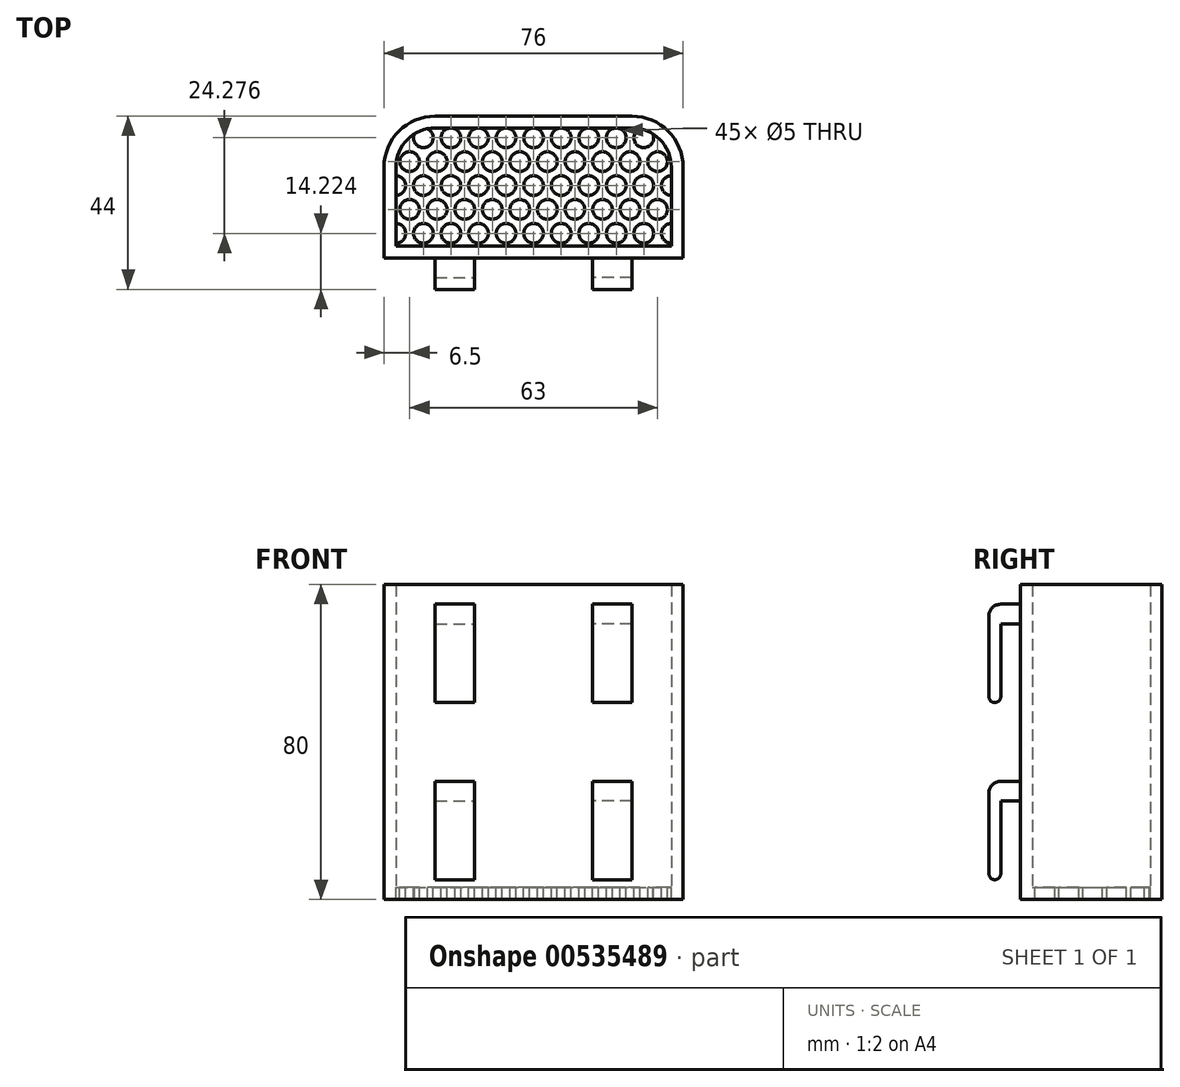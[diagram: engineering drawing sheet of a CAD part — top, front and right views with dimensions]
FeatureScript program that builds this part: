
annotation { "Feature Type Name" : "Feature", "Feature Type Description" : "" }
export const myFeature = defineFeature(function(context is Context, id is Id, definition is map)
    precondition{}
    {
        {
            var Q0;
            Q0=qCreatedBy(makeId("Top.planeOp"),FACE);
            var sketch = newSketch(context, id + "F0", { "sketchPlane" : qUnion([Q0])});
            skLineSegment(sketch, "E0.bottom", {"start": v(-35, -15) * mm, "end": v(35, -15) * mm});
            skLineSegment(sketch, "E0.top", {"start": v(-25, 15) * mm, "end": v(25, 15) * mm});
            skLineSegment(sketch, "E0.left", {"start": v(-35, -15) * mm, "end": v(-35, 5) * mm});
            skLineSegment(sketch, "E0.right", {"start": v(35, -15) * mm, "end": v(35, 5) * mm});
            skPoint(sketch, "E0.middle", {"position": v(0, 0) * mm});
            skPoint(sketch, "E1.visualSharp", {"position": v(-35, 15) * mm});
            skArc(sketch, "E1.filletArc", {"start": v(-25, 15) * mm, "mid": v(-32.07, 12.07) * mm, "end": v(-35, 5) * mm});
            skPoint(sketch, "E2.visualSharp", {"position": v(35, 15) * mm});
            skArc(sketch, "E2.filletArc", {"start": v(35, 5) * mm, "mid": v(32.07, 12.07) * mm, "end": v(25, 15) * mm});
            skLineSegment(sketch, "E3.0", {"start": v(-38, -18) * mm, "end": v(38, -18) * mm});
            skArc(sketch, "E3.1", {"start": v(-25, 18) * mm, "mid": v(-34.2, 14.2) * mm, "end": v(-38, 5) * mm});
            skLineSegment(sketch, "E3.2", {"start": v(-25, 18) * mm, "end": v(25, 18) * mm});
            skLineSegment(sketch, "E3.3", {"start": v(-38, -18) * mm, "end": v(-38, 5) * mm});
            skArc(sketch, "E3.4", {"start": v(38, 5) * mm, "mid": v(34.2, 14.2) * mm, "end": v(25, 18) * mm});
            skLineSegment(sketch, "E3.5", {"start": v(38, -18) * mm, "end": v(38, 5) * mm});
            skSolve(sketch);
        }
        {
            var Q0;
            Q0=makeQuery(id+"F0.imprint","IMPRINT",FACE,{"disambiguationData":[TD([[makeQuery(id+"F0.imprint","IMPRINT",EDGE,{"derivedFrom":sQuery(id+"F0.wireOp",EDGE,"E0.bottom")}),-1.0]])]});
            extrude(context, id + "F1", {"entities" : qUnion([Q0]), "depth" : 80 * mm, "offsetDistance" : 25 * mm});
        }
        {
            var Q0;
            Q0=makeQuery(id+"F0.imprint","IMPRINT",FACE,{"disambiguationData":[TD([[makeQuery(id+"F0.imprint","IMPRINT",EDGE,{"derivedFrom":sQuery(id+"F0.wireOp",EDGE,"E0.bottom")}),1.0]])]});
            extrude(context, id + "F2", {"entities" : qUnion([Q0]), "operationType" : NewBodyOperationType.ADD, "depth" : 3 * mm, "offsetDistance" : 25 * mm});
        }
        {
            var Q0;
            Q0=makeQuery(id+"F2.opExtrude","CAP_FACE",FACE,{"disambiguationData":[OSD([sQuery(id+"F0.wireOp",EDGE,"E0.bottom"),sQuery(id+"F0.wireOp",EDGE,"E0.top"),sQuery(id+"F0.wireOp",EDGE,"E0.left"),sQuery(id+"F0.wireOp",EDGE,"E0.right"),sQuery(id+"F0.wireOp",EDGE,"E1.filletArc"),sQuery(id+"F0.wireOp",EDGE,"E2.filletArc")])],"isStart":false});
            var sketch = newSketch(context, id + "F3", { "sketchPlane" : qUnion([Q0])});
            skCircle(sketch, "E4.1.0.0", {"center": v(-28, 12.5) * mm, "radius": 2.5 * mm});
            skCircle(sketch, "E4.2.0.0", {"center": v(-21, 12.5) * mm, "radius": 2.5 * mm});
            skCircle(sketch, "E4.3.0.0", {"center": v(-14, 12.5) * mm, "radius": 2.5 * mm});
            skCircle(sketch, "E4.4.0.0", {"center": v(-7, 12.5) * mm, "radius": 2.5 * mm});
            skCircle(sketch, "E4.5.0.0", {"center": v(0, 12.5) * mm, "radius": 2.5 * mm});
            skCircle(sketch, "E4.6.0.0", {"center": v(7, 12.5) * mm, "radius": 2.5 * mm});
            skCircle(sketch, "E4.7.0.0", {"center": v(14, 12.5) * mm, "radius": 2.5 * mm});
            skCircle(sketch, "E4.8.0.0", {"center": v(21, 12.5) * mm, "radius": 2.5 * mm});
            skLineSegment(sketch, "E4.direction1", {"start": v(-35, 12.5) * mm, "end": v(-28, 12.5) * mm, "construction": true});
            skCircle(sketch, "E5.0.9.0", {"center": v(28, 12.5) * mm, "radius": 2.5 * mm});
            skCircle(sketch, "E6.1.0.0", {"center": v(10.5, 6.44) * mm, "radius": 2.5 * mm});
            skCircle(sketch, "E6.1.0.1", {"center": v(-24.5, 6.44) * mm, "radius": 2.5 * mm});
            skCircle(sketch, "E6.1.0.2", {"center": v(-3.5, 6.44) * mm, "radius": 2.5 * mm});
            skCircle(sketch, "E6.1.0.3", {"center": v(24.5, 6.44) * mm, "radius": 2.5 * mm});
            skCircle(sketch, "E6.1.0.4", {"center": v(-17.5, 6.44) * mm, "radius": 2.5 * mm});
            skCircle(sketch, "E6.1.0.5", {"center": v(17.5, 6.44) * mm, "radius": 2.5 * mm});
            skCircle(sketch, "E6.1.0.6", {"center": v(3.5, 6.44) * mm, "radius": 2.5 * mm});
            skCircle(sketch, "E6.1.0.8", {"center": v(-31.5, 6.44) * mm, "radius": 2.5 * mm});
            skCircle(sketch, "E6.1.0.9", {"center": v(31.5, 6.44) * mm, "radius": 2.5 * mm});
            skCircle(sketch, "E6.1.0.10", {"center": v(-10.5, 6.44) * mm, "radius": 2.5 * mm});
            skLineSegment(sketch, "E6.1.0.11", {"start": v(-31.5, 6.44) * mm, "end": v(-24.5, 6.44) * mm, "construction": true});
            skLineSegment(sketch, "E6.direction1", {"start": v(-35, 12.5) * mm, "end": v(-31.5, 6.44) * mm, "construction": true});
            skLineSegment(sketch, "E7", {"start": v(-3.5, 6.44) * mm, "end": v(3.5, 6.44) * mm, "construction": true});
            skLineSegment(sketch, "E8", {"start": v(-31.5, 6.44) * mm, "end": v(-28, 12.5) * mm, "construction": true});
            skCircle(sketch, "E9.1.0.0", {"center": v(31.5, -5.7) * mm, "radius": 2.5 * mm});
            skLineSegment(sketch, "E9.1.0.1", {"start": v(-31.5, -5.7) * mm, "end": v(-24.5, -5.7) * mm, "construction": true});
            skCircle(sketch, "E9.1.0.2", {"center": v(28, 0.36) * mm, "radius": 2.5 * mm});
            skLineSegment(sketch, "E9.1.0.3", {"start": v(-35, 0.36) * mm, "end": v(-28, 0.36) * mm, "construction": true});
            skCircle(sketch, "E9.1.0.4", {"center": v(-14, 0.36) * mm, "radius": 2.5 * mm});
            skCircle(sketch, "E9.1.0.5", {"center": v(-31.5, -5.7) * mm, "radius": 2.5 * mm});
            skCircle(sketch, "E9.1.0.6", {"center": v(-7, 0.36) * mm, "radius": 2.5 * mm});
            skCircle(sketch, "E9.1.0.7", {"center": v(0, 0.36) * mm, "radius": 2.5 * mm});
            skCircle(sketch, "E9.1.0.8", {"center": v(35, 0.36) * mm, "radius": 2.5 * mm});
            skCircle(sketch, "E9.1.0.9", {"center": v(10.5, -5.7) * mm, "radius": 2.5 * mm});
            skCircle(sketch, "E9.1.0.10", {"center": v(-21, 0.36) * mm, "radius": 2.5 * mm});
            skCircle(sketch, "E9.1.0.11", {"center": v(-28, 0.36) * mm, "radius": 2.5 * mm});
            skCircle(sketch, "E9.1.0.12", {"center": v(-10.5, -5.7) * mm, "radius": 2.5 * mm});
            skCircle(sketch, "E9.1.0.13", {"center": v(17.5, -5.7) * mm, "radius": 2.5 * mm});
            skCircle(sketch, "E9.1.0.14", {"center": v(-24.5, -5.7) * mm, "radius": 2.5 * mm});
            skCircle(sketch, "E9.1.0.15", {"center": v(7, 0.36) * mm, "radius": 2.5 * mm});
            skCircle(sketch, "E9.1.0.16", {"center": v(-3.5, -5.7) * mm, "radius": 2.5 * mm});
            skLineSegment(sketch, "E9.1.0.17", {"start": v(-3.5, -5.7) * mm, "end": v(3.5, -5.7) * mm, "construction": true});
            skCircle(sketch, "E9.1.0.18", {"center": v(24.5, -5.7) * mm, "radius": 2.5 * mm});
            skCircle(sketch, "E9.1.0.19", {"center": v(-35, 0.36) * mm, "radius": 2.5 * mm});
            skCircle(sketch, "E9.1.0.20", {"center": v(14, 0.36) * mm, "radius": 2.5 * mm});
            skCircle(sketch, "E9.1.0.21", {"center": v(21, 0.36) * mm, "radius": 2.5 * mm});
            skCircle(sketch, "E9.1.0.22", {"center": v(3.5, -5.7) * mm, "radius": 2.5 * mm});
            skCircle(sketch, "E9.1.0.23", {"center": v(-17.5, -5.7) * mm, "radius": 2.5 * mm});
            skLineSegment(sketch, "E9.1.0.24", {"start": v(-31.5, -5.7) * mm, "end": v(-28, 0.36) * mm, "construction": true});
            skLineSegment(sketch, "E9.1.0.25", {"start": v(-35, 0.36) * mm, "end": v(-31.5, -5.7) * mm, "construction": true});
            skCircle(sketch, "E9.2.0.2", {"center": v(28, -11.78) * mm, "radius": 2.5 * mm});
            skLineSegment(sketch, "E9.2.0.3", {"start": v(-35, -11.78) * mm, "end": v(-28, -11.78) * mm, "construction": true});
            skCircle(sketch, "E9.2.0.4", {"center": v(-14, -11.78) * mm, "radius": 2.5 * mm});
            skCircle(sketch, "E9.2.0.6", {"center": v(-7, -11.78) * mm, "radius": 2.5 * mm});
            skCircle(sketch, "E9.2.0.7", {"center": v(0, -11.78) * mm, "radius": 2.5 * mm});
            skCircle(sketch, "E9.2.0.8", {"center": v(35, -11.78) * mm, "radius": 2.5 * mm});
            skCircle(sketch, "E9.2.0.10", {"center": v(-21, -11.78) * mm, "radius": 2.5 * mm});
            skCircle(sketch, "E9.2.0.11", {"center": v(-28, -11.78) * mm, "radius": 2.5 * mm});
            skCircle(sketch, "E9.2.0.15", {"center": v(7, -11.78) * mm, "radius": 2.5 * mm});
            skCircle(sketch, "E9.2.0.19", {"center": v(-35, -11.78) * mm, "radius": 2.5 * mm});
            skCircle(sketch, "E9.2.0.20", {"center": v(14, -11.78) * mm, "radius": 2.5 * mm});
            skCircle(sketch, "E9.2.0.21", {"center": v(21, -11.78) * mm, "radius": 2.5 * mm});
            skLineSegment(sketch, "E9.direction1", {"start": v(-31.5, 6.44) * mm, "end": v(-31.5, -5.7) * mm, "construction": true});
            skSolve(sketch);
        }
        {
            var Q0;
            {var subQ0=sQuery(id+"F3.wireOp",EDGE,"E4.1.0.0");var subQ1=makeQuery(id+"F2.opExtrude","CAP_EDGE",EDGE,{"disambiguationData":[OSD([sQuery(id+"F0.wireOp",EDGE,"E1.filletArc")])],"isStart":false});var subQ2=makeQuery(id+"F3.imprint","INTERSECT",VERTEX,{"disambiguationData":[OD(0.0)],"derivedFrom":[subQ1,subQ0]});Q0=makeQuery(id+"F3.imprint","IMPRINT",FACE,{"disambiguationData":[TD([[makeQuery(id+"F3.imprint","IMPRINT",EDGE,{"disambiguationData":[TD([[subQ2,1.0]])],"derivedFrom":subQ0}),1.0]])]});}
            var Q1;
            Q1=makeQuery(id+"F3.imprint","IMPRINT",FACE,{"disambiguationData":[TD([[makeQuery(id+"F3.imprint","IMPRINT",EDGE,{"derivedFrom":sQuery(id+"F3.wireOp",EDGE,"E6.1.0.8")}),1.0]])]});
            var Q2;
            Q2=makeQuery(id+"F3.imprint","IMPRINT",FACE,{"disambiguationData":[TD([[makeQuery(id+"F3.imprint","IMPRINT",EDGE,{"derivedFrom":sQuery(id+"F3.wireOp",EDGE,"E9.1.0.11")}),1.0]])]});
            var Q3;
            {var subQ0=sQuery(id+"F3.wireOp",EDGE,"E9.1.0.19");var subQ1=makeQuery(id+"F2.opExtrude","CAP_EDGE",EDGE,{"disambiguationData":[OSD([sQuery(id+"F0.wireOp",EDGE,"E0.left")])],"isStart":false});var subQ2=makeQuery(id+"F3.imprint","INTERSECT",VERTEX,{"disambiguationData":[OD(0.0)],"derivedFrom":[subQ1,subQ0]});Q3=makeQuery(id+"F3.imprint","IMPRINT",FACE,{"disambiguationData":[TD([[makeQuery(id+"F3.imprint","IMPRINT",EDGE,{"disambiguationData":[TD([[subQ2,1.0]])],"derivedFrom":subQ0}),1.0]])]});}
            var Q4;
            Q4=makeQuery(id+"F3.imprint","IMPRINT",FACE,{"disambiguationData":[TD([[makeQuery(id+"F3.imprint","IMPRINT",EDGE,{"derivedFrom":sQuery(id+"F3.wireOp",EDGE,"E9.1.0.5")}),1.0]])]});
            var Q5;
            {var subQ0=sQuery(id+"F3.wireOp",EDGE,"E9.2.0.19");var subQ1=makeQuery(id+"F2.opExtrude","CAP_EDGE",EDGE,{"disambiguationData":[OSD([sQuery(id+"F0.wireOp",EDGE,"E0.left")])],"isStart":false});var subQ2=makeQuery(id+"F3.imprint","INTERSECT",VERTEX,{"disambiguationData":[OD(0.0)],"derivedFrom":[subQ1,subQ0]});Q5=makeQuery(id+"F3.imprint","IMPRINT",FACE,{"disambiguationData":[TD([[makeQuery(id+"F3.imprint","IMPRINT",EDGE,{"disambiguationData":[TD([[subQ2,-1.0]])],"derivedFrom":subQ0}),1.0]])]});}
            var Q6;
            Q6=makeQuery(id+"F3.imprint","IMPRINT",FACE,{"disambiguationData":[TD([[makeQuery(id+"F3.imprint","IMPRINT",EDGE,{"derivedFrom":sQuery(id+"F3.wireOp",EDGE,"E9.2.0.11")}),1.0]])]});
            var Q7;
            Q7=makeQuery(id+"F3.imprint","IMPRINT",FACE,{"disambiguationData":[TD([[makeQuery(id+"F3.imprint","IMPRINT",EDGE,{"derivedFrom":sQuery(id+"F3.wireOp",EDGE,"E9.1.0.14")}),1.0]])]});
            var Q8;
            Q8=makeQuery(id+"F3.imprint","IMPRINT",FACE,{"disambiguationData":[TD([[makeQuery(id+"F3.imprint","IMPRINT",EDGE,{"derivedFrom":sQuery(id+"F3.wireOp",EDGE,"E9.1.0.10")}),1.0]])]});
            var Q9;
            Q9=makeQuery(id+"F3.imprint","IMPRINT",FACE,{"disambiguationData":[TD([[makeQuery(id+"F3.imprint","IMPRINT",EDGE,{"derivedFrom":sQuery(id+"F3.wireOp",EDGE,"E6.1.0.1")}),1.0]])]});
            var Q10;
            Q10=makeQuery(id+"F3.imprint","IMPRINT",FACE,{"disambiguationData":[TD([[makeQuery(id+"F3.imprint","IMPRINT",EDGE,{"derivedFrom":sQuery(id+"F3.wireOp",EDGE,"E4.2.0.0")}),1.0]])]});
            var Q11;
            Q11=makeQuery(id+"F3.imprint","IMPRINT",FACE,{"disambiguationData":[TD([[makeQuery(id+"F3.imprint","IMPRINT",EDGE,{"derivedFrom":sQuery(id+"F3.wireOp",EDGE,"E4.3.0.0")}),1.0]])]});
            var Q12;
            Q12=makeQuery(id+"F3.imprint","IMPRINT",FACE,{"disambiguationData":[TD([[makeQuery(id+"F3.imprint","IMPRINT",EDGE,{"derivedFrom":sQuery(id+"F3.wireOp",EDGE,"E4.4.0.0")}),1.0]])]});
            var Q13;
            Q13=makeQuery(id+"F3.imprint","IMPRINT",FACE,{"disambiguationData":[TD([[makeQuery(id+"F3.imprint","IMPRINT",EDGE,{"derivedFrom":sQuery(id+"F3.wireOp",EDGE,"E4.5.0.0")}),1.0]])]});
            var Q14;
            Q14=makeQuery(id+"F3.imprint","IMPRINT",FACE,{"disambiguationData":[TD([[makeQuery(id+"F3.imprint","IMPRINT",EDGE,{"derivedFrom":sQuery(id+"F3.wireOp",EDGE,"E4.6.0.0")}),1.0]])]});
            var Q15;
            Q15=makeQuery(id+"F3.imprint","IMPRINT",FACE,{"disambiguationData":[TD([[makeQuery(id+"F3.imprint","IMPRINT",EDGE,{"derivedFrom":sQuery(id+"F3.wireOp",EDGE,"E4.7.0.0")}),1.0]])]});
            var Q16;
            Q16=makeQuery(id+"F3.imprint","IMPRINT",FACE,{"disambiguationData":[TD([[makeQuery(id+"F3.imprint","IMPRINT",EDGE,{"derivedFrom":sQuery(id+"F3.wireOp",EDGE,"E4.8.0.0")}),1.0]])]});
            var Q17;
            {var subQ0=sQuery(id+"F3.wireOp",EDGE,"E5.0.9.0");var subQ1=makeQuery(id+"F2.opExtrude","CAP_EDGE",EDGE,{"disambiguationData":[OSD([sQuery(id+"F0.wireOp",EDGE,"E2.filletArc")])],"isStart":false});var subQ2=makeQuery(id+"F3.imprint","INTERSECT",VERTEX,{"disambiguationData":[OD(0.0)],"derivedFrom":[subQ1,subQ0]});Q17=makeQuery(id+"F3.imprint","IMPRINT",FACE,{"disambiguationData":[TD([[makeQuery(id+"F3.imprint","IMPRINT",EDGE,{"disambiguationData":[TD([[subQ2,-1.0]])],"derivedFrom":subQ0}),1.0]])]});}
            var Q18;
            Q18=makeQuery(id+"F3.imprint","IMPRINT",FACE,{"disambiguationData":[TD([[makeQuery(id+"F3.imprint","IMPRINT",EDGE,{"derivedFrom":sQuery(id+"F3.wireOp",EDGE,"E6.1.0.3")}),1.0]])]});
            var Q19;
            Q19=makeQuery(id+"F3.imprint","IMPRINT",FACE,{"disambiguationData":[TD([[makeQuery(id+"F3.imprint","IMPRINT",EDGE,{"derivedFrom":sQuery(id+"F3.wireOp",EDGE,"E6.1.0.9")}),1.0]])]});
            var Q20;
            {var subQ0=sQuery(id+"F3.wireOp",EDGE,"E9.1.0.8");var subQ1=makeQuery(id+"F2.opExtrude","CAP_EDGE",EDGE,{"disambiguationData":[OSD([sQuery(id+"F0.wireOp",EDGE,"E0.right")])],"isStart":false});var subQ2=makeQuery(id+"F3.imprint","INTERSECT",VERTEX,{"disambiguationData":[OD(0.0)],"derivedFrom":[subQ1,subQ0]});Q20=makeQuery(id+"F3.imprint","IMPRINT",FACE,{"disambiguationData":[TD([[makeQuery(id+"F3.imprint","IMPRINT",EDGE,{"disambiguationData":[TD([[subQ2,-1.0]])],"derivedFrom":subQ0}),1.0]])]});}
            var Q21;
            Q21=makeQuery(id+"F3.imprint","IMPRINT",FACE,{"disambiguationData":[TD([[makeQuery(id+"F3.imprint","IMPRINT",EDGE,{"derivedFrom":sQuery(id+"F3.wireOp",EDGE,"E9.1.0.0")}),1.0]])]});
            var Q22;
            {var subQ0=sQuery(id+"F3.wireOp",EDGE,"E9.2.0.8");var subQ1=makeQuery(id+"F2.opExtrude","CAP_EDGE",EDGE,{"disambiguationData":[OSD([sQuery(id+"F0.wireOp",EDGE,"E0.right")])],"isStart":false});var subQ2=makeQuery(id+"F3.imprint","INTERSECT",VERTEX,{"disambiguationData":[OD(0.0)],"derivedFrom":[subQ1,subQ0]});Q22=makeQuery(id+"F3.imprint","IMPRINT",FACE,{"disambiguationData":[TD([[makeQuery(id+"F3.imprint","IMPRINT",EDGE,{"disambiguationData":[TD([[subQ2,1.0]])],"derivedFrom":subQ0}),1.0]])]});}
            var Q23;
            Q23=makeQuery(id+"F3.imprint","IMPRINT",FACE,{"disambiguationData":[TD([[makeQuery(id+"F3.imprint","IMPRINT",EDGE,{"derivedFrom":sQuery(id+"F3.wireOp",EDGE,"E9.2.0.2")}),1.0]])]});
            var Q24;
            Q24=makeQuery(id+"F3.imprint","IMPRINT",FACE,{"disambiguationData":[TD([[makeQuery(id+"F3.imprint","IMPRINT",EDGE,{"derivedFrom":sQuery(id+"F3.wireOp",EDGE,"E9.2.0.21")}),1.0]])]});
            var Q25;
            Q25=makeQuery(id+"F3.imprint","IMPRINT",FACE,{"disambiguationData":[TD([[makeQuery(id+"F3.imprint","IMPRINT",EDGE,{"derivedFrom":sQuery(id+"F3.wireOp",EDGE,"E9.2.0.20")}),1.0]])]});
            var Q26;
            Q26=makeQuery(id+"F3.imprint","IMPRINT",FACE,{"disambiguationData":[TD([[makeQuery(id+"F3.imprint","IMPRINT",EDGE,{"derivedFrom":sQuery(id+"F3.wireOp",EDGE,"E9.2.0.15")}),1.0]])]});
            var Q27;
            Q27=makeQuery(id+"F3.imprint","IMPRINT",FACE,{"disambiguationData":[TD([[makeQuery(id+"F3.imprint","IMPRINT",EDGE,{"derivedFrom":sQuery(id+"F3.wireOp",EDGE,"E9.2.0.7")}),1.0]])]});
            var Q28;
            Q28=makeQuery(id+"F3.imprint","IMPRINT",FACE,{"disambiguationData":[TD([[makeQuery(id+"F3.imprint","IMPRINT",EDGE,{"derivedFrom":sQuery(id+"F3.wireOp",EDGE,"E9.2.0.6")}),1.0]])]});
            var Q29;
            Q29=makeQuery(id+"F3.imprint","IMPRINT",FACE,{"disambiguationData":[TD([[makeQuery(id+"F3.imprint","IMPRINT",EDGE,{"derivedFrom":sQuery(id+"F3.wireOp",EDGE,"E9.2.0.4")}),1.0]])]});
            var Q30;
            Q30=makeQuery(id+"F3.imprint","IMPRINT",FACE,{"disambiguationData":[TD([[makeQuery(id+"F3.imprint","IMPRINT",EDGE,{"derivedFrom":sQuery(id+"F3.wireOp",EDGE,"E9.2.0.10")}),1.0]])]});
            var Q31;
            Q31=makeQuery(id+"F3.imprint","IMPRINT",FACE,{"disambiguationData":[TD([[makeQuery(id+"F3.imprint","IMPRINT",EDGE,{"derivedFrom":sQuery(id+"F3.wireOp",EDGE,"E9.1.0.23")}),1.0]])]});
            var Q32;
            Q32=makeQuery(id+"F3.imprint","IMPRINT",FACE,{"disambiguationData":[TD([[makeQuery(id+"F3.imprint","IMPRINT",EDGE,{"derivedFrom":sQuery(id+"F3.wireOp",EDGE,"E9.1.0.12")}),1.0]])]});
            var Q33;
            Q33=makeQuery(id+"F3.imprint","IMPRINT",FACE,{"disambiguationData":[TD([[makeQuery(id+"F3.imprint","IMPRINT",EDGE,{"derivedFrom":sQuery(id+"F3.wireOp",EDGE,"E9.1.0.16")}),1.0]])]});
            var Q34;
            Q34=makeQuery(id+"F3.imprint","IMPRINT",FACE,{"disambiguationData":[TD([[makeQuery(id+"F3.imprint","IMPRINT",EDGE,{"derivedFrom":sQuery(id+"F3.wireOp",EDGE,"E9.1.0.22")}),1.0]])]});
            var Q35;
            Q35=makeQuery(id+"F3.imprint","IMPRINT",FACE,{"disambiguationData":[TD([[makeQuery(id+"F3.imprint","IMPRINT",EDGE,{"derivedFrom":sQuery(id+"F3.wireOp",EDGE,"E9.1.0.9")}),1.0]])]});
            var Q36;
            Q36=makeQuery(id+"F3.imprint","IMPRINT",FACE,{"disambiguationData":[TD([[makeQuery(id+"F3.imprint","IMPRINT",EDGE,{"derivedFrom":sQuery(id+"F3.wireOp",EDGE,"E9.1.0.13")}),1.0]])]});
            var Q37;
            Q37=makeQuery(id+"F3.imprint","IMPRINT",FACE,{"disambiguationData":[TD([[makeQuery(id+"F3.imprint","IMPRINT",EDGE,{"derivedFrom":sQuery(id+"F3.wireOp",EDGE,"E9.1.0.18")}),1.0]])]});
            var Q38;
            Q38=makeQuery(id+"F3.imprint","IMPRINT",FACE,{"disambiguationData":[TD([[makeQuery(id+"F3.imprint","IMPRINT",EDGE,{"derivedFrom":sQuery(id+"F3.wireOp",EDGE,"E9.1.0.2")}),1.0]])]});
            var Q39;
            Q39=makeQuery(id+"F3.imprint","IMPRINT",FACE,{"disambiguationData":[TD([[makeQuery(id+"F3.imprint","IMPRINT",EDGE,{"derivedFrom":sQuery(id+"F3.wireOp",EDGE,"E9.1.0.21")}),1.0]])]});
            var Q40;
            Q40=makeQuery(id+"F3.imprint","IMPRINT",FACE,{"disambiguationData":[TD([[makeQuery(id+"F3.imprint","IMPRINT",EDGE,{"derivedFrom":sQuery(id+"F3.wireOp",EDGE,"E9.1.0.20")}),1.0]])]});
            var Q41;
            Q41=makeQuery(id+"F3.imprint","IMPRINT",FACE,{"disambiguationData":[TD([[makeQuery(id+"F3.imprint","IMPRINT",EDGE,{"derivedFrom":sQuery(id+"F3.wireOp",EDGE,"E9.1.0.15")}),1.0]])]});
            var Q42;
            Q42=makeQuery(id+"F3.imprint","IMPRINT",FACE,{"disambiguationData":[TD([[makeQuery(id+"F3.imprint","IMPRINT",EDGE,{"derivedFrom":sQuery(id+"F3.wireOp",EDGE,"E9.1.0.7")}),1.0]])]});
            var Q43;
            Q43=makeQuery(id+"F3.imprint","IMPRINT",FACE,{"disambiguationData":[TD([[makeQuery(id+"F3.imprint","IMPRINT",EDGE,{"derivedFrom":sQuery(id+"F3.wireOp",EDGE,"E9.1.0.6")}),1.0]])]});
            var Q44;
            Q44=makeQuery(id+"F3.imprint","IMPRINT",FACE,{"disambiguationData":[TD([[makeQuery(id+"F3.imprint","IMPRINT",EDGE,{"derivedFrom":sQuery(id+"F3.wireOp",EDGE,"E9.1.0.4")}),1.0]])]});
            var Q45;
            Q45=makeQuery(id+"F3.imprint","IMPRINT",FACE,{"disambiguationData":[TD([[makeQuery(id+"F3.imprint","IMPRINT",EDGE,{"derivedFrom":sQuery(id+"F3.wireOp",EDGE,"E6.1.0.4")}),1.0]])]});
            var Q46;
            Q46=makeQuery(id+"F3.imprint","IMPRINT",FACE,{"disambiguationData":[TD([[makeQuery(id+"F3.imprint","IMPRINT",EDGE,{"derivedFrom":sQuery(id+"F3.wireOp",EDGE,"E6.1.0.10")}),1.0]])]});
            var Q47;
            Q47=makeQuery(id+"F3.imprint","IMPRINT",FACE,{"disambiguationData":[TD([[makeQuery(id+"F3.imprint","IMPRINT",EDGE,{"derivedFrom":sQuery(id+"F3.wireOp",EDGE,"E6.1.0.2")}),1.0]])]});
            var Q48;
            Q48=makeQuery(id+"F3.imprint","IMPRINT",FACE,{"disambiguationData":[TD([[makeQuery(id+"F3.imprint","IMPRINT",EDGE,{"derivedFrom":sQuery(id+"F3.wireOp",EDGE,"E6.1.0.6")}),1.0]])]});
            var Q49;
            Q49=makeQuery(id+"F3.imprint","IMPRINT",FACE,{"disambiguationData":[TD([[makeQuery(id+"F3.imprint","IMPRINT",EDGE,{"derivedFrom":sQuery(id+"F3.wireOp",EDGE,"E6.1.0.0")}),1.0]])]});
            var Q50;
            Q50=makeQuery(id+"F3.imprint","IMPRINT",FACE,{"disambiguationData":[TD([[makeQuery(id+"F3.imprint","IMPRINT",EDGE,{"derivedFrom":sQuery(id+"F3.wireOp",EDGE,"E6.1.0.5")}),1.0]])]});
            extrude(context, id + "F4", {"entities" : qUnion([Q0, Q1, Q2, Q3, Q4, Q5, Q6, Q7, Q8, Q9, Q10, Q11, Q12, Q13, Q14, Q15, Q16, Q17, Q18, Q19, Q20, Q21, Q22, Q23, Q24, Q25, Q26, Q27, Q28, Q29, Q30, Q31, Q32, Q33, Q34, Q35, Q36, Q37, Q38, Q39, Q40, Q41, Q42, Q43, Q44, Q45, Q46, Q47, Q48, Q49, Q50]), "operationType" : NewBodyOperationType.REMOVE, "oppositeDirection" : true, "depth" : 3 * mm, "offsetDistance" : 25 * mm});
        }
        {
            var Q0;
            Q0=makeQuery(id+"F1.opExtrude","SWEPT_FACE",FACE,{"disambiguationData":[OSD([sQuery(id+"F0.wireOp",EDGE,"E3.0")])]});
            var sketch = newSketch(context, id + "F5", { "sketchPlane" : qUnion([Q0])});
            skLineSegment(sketch, "E10", {"start": v(0, 0) * mm, "end": v(0, 80) * mm, "construction": true});
            skLineSegment(sketch, "E11.bottom", {"start": v(-25, 75) * mm, "end": v(-15, 75) * mm});
            skLineSegment(sketch, "E11.top", {"start": v(-25, 70) * mm, "end": v(-15, 70) * mm});
            skLineSegment(sketch, "E11.left", {"start": v(-25, 75) * mm, "end": v(-25, 70) * mm});
            skLineSegment(sketch, "E11.right", {"start": v(-15, 75) * mm, "end": v(-15, 70) * mm});
            skLineSegment(sketch, "E12.MirrorCS", {"start": v(15, 75) * mm, "end": v(15, 70) * mm});
            skLineSegment(sketch, "E13.MirrorCS", {"start": v(25, 75) * mm, "end": v(25, 70) * mm});
            skLineSegment(sketch, "E14.MirrorCS", {"start": v(25, 70) * mm, "end": v(15, 70) * mm});
            skLineSegment(sketch, "E15.MirrorCS", {"start": v(25, 75) * mm, "end": v(15, 75) * mm});
            skLineSegment(sketch, "E16.0.1.0", {"start": v(25, 30) * mm, "end": v(15, 30) * mm});
            skLineSegment(sketch, "E16.0.1.1", {"start": v(-15, 30) * mm, "end": v(-15, 25) * mm});
            skLineSegment(sketch, "E16.0.1.2", {"start": v(15, 30) * mm, "end": v(15, 25) * mm});
            skLineSegment(sketch, "E16.0.1.3", {"start": v(25, 30) * mm, "end": v(25, 25) * mm});
            skLineSegment(sketch, "E16.0.1.4", {"start": v(-25, 30) * mm, "end": v(-15, 30) * mm});
            skLineSegment(sketch, "E16.0.1.5", {"start": v(25, 25) * mm, "end": v(15, 25) * mm});
            skLineSegment(sketch, "E16.0.1.6", {"start": v(-25, 30) * mm, "end": v(-25, 25) * mm});
            skLineSegment(sketch, "E16.0.1.7", {"start": v(-25, 25) * mm, "end": v(-15, 25) * mm});
            skLineSegment(sketch, "E16.direction1", {"start": v(-25, 70) * mm, "end": v(0, 70) * mm, "construction": true});
            skLineSegment(sketch, "E16.direction2", {"start": v(-25, 70) * mm, "end": v(-25, 25) * mm, "construction": true});
            skSolve(sketch);
        }
        {
            var Q0;
            Q0 = qSketchRegion(id + "F5", true);
            extrude(context, id + "F6", {"entities" : qUnion([Q0]), "operationType" : NewBodyOperationType.ADD, "depth" : 5 * mm, "offsetDistance" : 25 * mm});
        }
        {
            var Q0;
            Q0=makeQuery(id+"F6.opExtrude","CAP_FACE",FACE,{"disambiguationData":[OSD([sQuery(id+"F5.wireOp",EDGE,"E11.bottom"),sQuery(id+"F5.wireOp",EDGE,"E11.top"),sQuery(id+"F5.wireOp",EDGE,"E11.left"),sQuery(id+"F5.wireOp",EDGE,"E11.right")])],"isStart":false});
            var sketch = newSketch(context, id + "F7", { "sketchPlane" : qUnion([Q0])});
            skLineSegment(sketch, "E17.bottom", {"start": v(-25, 75) * mm, "end": v(-15, 75) * mm});
            skLineSegment(sketch, "E17.top", {"start": v(-25, 50) * mm, "end": v(-15, 50) * mm});
            skLineSegment(sketch, "E17.left", {"start": v(-25, 75) * mm, "end": v(-25, 50) * mm});
            skLineSegment(sketch, "E17.right", {"start": v(-15, 75) * mm, "end": v(-15, 50) * mm});
            skLineSegment(sketch, "E18", {"start": v(0, 80) * mm, "end": v(0, 0) * mm, "construction": true});
            skLineSegment(sketch, "E19.MirrorCS", {"start": v(15, 75) * mm, "end": v(15, 50) * mm});
            skLineSegment(sketch, "E20.MirrorCS", {"start": v(25, 75) * mm, "end": v(25, 50) * mm});
            skLineSegment(sketch, "E21.MirrorCS", {"start": v(25, 50) * mm, "end": v(15, 50) * mm});
            skLineSegment(sketch, "E22.MirrorCS", {"start": v(25, 75) * mm, "end": v(15, 75) * mm});
            skLineSegment(sketch, "E23.0.1.0", {"start": v(25, 5) * mm, "end": v(15, 5) * mm});
            skLineSegment(sketch, "E23.0.1.1", {"start": v(25, 30) * mm, "end": v(25, 5) * mm});
            skLineSegment(sketch, "E23.0.1.2", {"start": v(15, 30) * mm, "end": v(15, 5) * mm});
            skLineSegment(sketch, "E23.0.1.3", {"start": v(25, 30) * mm, "end": v(15, 30) * mm});
            skLineSegment(sketch, "E23.0.1.4", {"start": v(-15, 30) * mm, "end": v(-15, 5) * mm});
            skLineSegment(sketch, "E23.0.1.5", {"start": v(-25, 30) * mm, "end": v(-25, 5) * mm});
            skLineSegment(sketch, "E23.0.1.6", {"start": v(-25, 5) * mm, "end": v(-15, 5) * mm});
            skLineSegment(sketch, "E23.0.1.7", {"start": v(-25, 30) * mm, "end": v(-15, 30) * mm});
            skLineSegment(sketch, "E23.direction1", {"start": v(-25, 50) * mm, "end": v(0, 50) * mm, "construction": true});
            skLineSegment(sketch, "E23.direction2", {"start": v(-25, 50) * mm, "end": v(-25, 5) * mm, "construction": true});
            skSolve(sketch);
        }
        {
            var Q0;
            Q0 = qSketchRegion(id + "F7", true);
            extrude(context, id + "F8", {"entities" : qUnion([Q0]), "operationType" : NewBodyOperationType.ADD, "depth" : 3 * mm, "offsetDistance" : 25 * mm});
        }
        {
            var Q0;
            Q0=makeQuery(id+"F8.opExtrude","CAP_EDGE",EDGE,{"disambiguationData":[OSD([sQuery(id+"F7.wireOp",EDGE,"E23.0.1.7")])],"isStart":false});
            var Q1;
            Q1=makeQuery(id+"F8.opExtrude","CAP_EDGE",EDGE,{"disambiguationData":[OSD([sQuery(id+"F7.wireOp",EDGE,"E23.0.1.3")])],"isStart":false});
            var Q2;
            Q2=makeQuery(id+"F8.opExtrude","CAP_EDGE",EDGE,{"disambiguationData":[OSD([sQuery(id+"F7.wireOp",EDGE,"E17.bottom")])],"isStart":false});
            var Q3;
            Q3=makeQuery(id+"F8.opExtrude","CAP_EDGE",EDGE,{"disambiguationData":[OSD([sQuery(id+"F7.wireOp",EDGE,"E22.MirrorCS")])],"isStart":false});
            var Q4;
            Q4=makeQuery(id+"F6.opExtrude","CAP_EDGE",EDGE,{"disambiguationData":[OSD([sQuery(id+"F5.wireOp",EDGE,"E16.0.1.5")])],"isStart":false});
            var Q5;
            Q5=makeQuery(id+"F6.opExtrude","CAP_EDGE",EDGE,{"disambiguationData":[OSD([sQuery(id+"F5.wireOp",EDGE,"E14.MirrorCS")])],"isStart":false});
            var Q6;
            Q6=makeQuery(id+"F6.opExtrude","CAP_EDGE",EDGE,{"disambiguationData":[OSD([sQuery(id+"F5.wireOp",EDGE,"E11.top")])],"isStart":false});
            var Q7;
            Q7=makeQuery(id+"F6.opExtrude","CAP_EDGE",EDGE,{"disambiguationData":[OSD([sQuery(id+"F5.wireOp",EDGE,"E16.0.1.7")])],"isStart":false});
            fillet(context, id + "F9", {"entities" : qUnion([Q0, Q1, Q2, Q3, Q4, Q5, Q6, Q7]), "radius" : 3 * mm, "tangentPropagation" : true, "allowEdgeOverflow" : false});
        }
        {
            var Q0;
            Q0=makeQuery(id+"F8.opExtrude","CAP_EDGE",EDGE,{"disambiguationData":[OSD([sQuery(id+"F7.wireOp",EDGE,"E21.MirrorCS")])],"isStart":false});
            var Q1;
            Q1=makeQuery(id+"F8.opExtrude","CAP_EDGE",EDGE,{"disambiguationData":[OSD([sQuery(id+"F7.wireOp",EDGE,"E21.MirrorCS")])],"isStart":true});
            var Q2;
            Q2=makeQuery(id+"F8.opExtrude","CAP_EDGE",EDGE,{"disambiguationData":[OSD([sQuery(id+"F7.wireOp",EDGE,"E23.0.1.0")])],"isStart":true});
            var Q3;
            Q3=makeQuery(id+"F8.opExtrude","CAP_EDGE",EDGE,{"disambiguationData":[OSD([sQuery(id+"F7.wireOp",EDGE,"E17.top")])],"isStart":false});
            var Q4;
            Q4=makeQuery(id+"F8.opExtrude","CAP_EDGE",EDGE,{"disambiguationData":[OSD([sQuery(id+"F7.wireOp",EDGE,"E17.top")])],"isStart":true});
            var Q5;
            Q5=makeQuery(id+"F8.opExtrude","CAP_EDGE",EDGE,{"disambiguationData":[OSD([sQuery(id+"F7.wireOp",EDGE,"E23.0.1.6")])],"isStart":true});
            var Q6;
            Q6=makeQuery(id+"F8.opExtrude","CAP_EDGE",EDGE,{"disambiguationData":[OSD([sQuery(id+"F7.wireOp",EDGE,"E23.0.1.6")])],"isStart":false});
            var Q7;
            Q7=makeQuery(id+"F8.opExtrude","CAP_EDGE",EDGE,{"disambiguationData":[OSD([sQuery(id+"F7.wireOp",EDGE,"E23.0.1.0")])],"isStart":false});
            fillet(context, id + "F10", {"entities" : qUnion([Q0, Q1, Q2, Q3, Q4, Q5, Q6, Q7]), "radius" : 1.5 * mm, "tangentPropagation" : true, "allowEdgeOverflow" : false});
        }
    });
